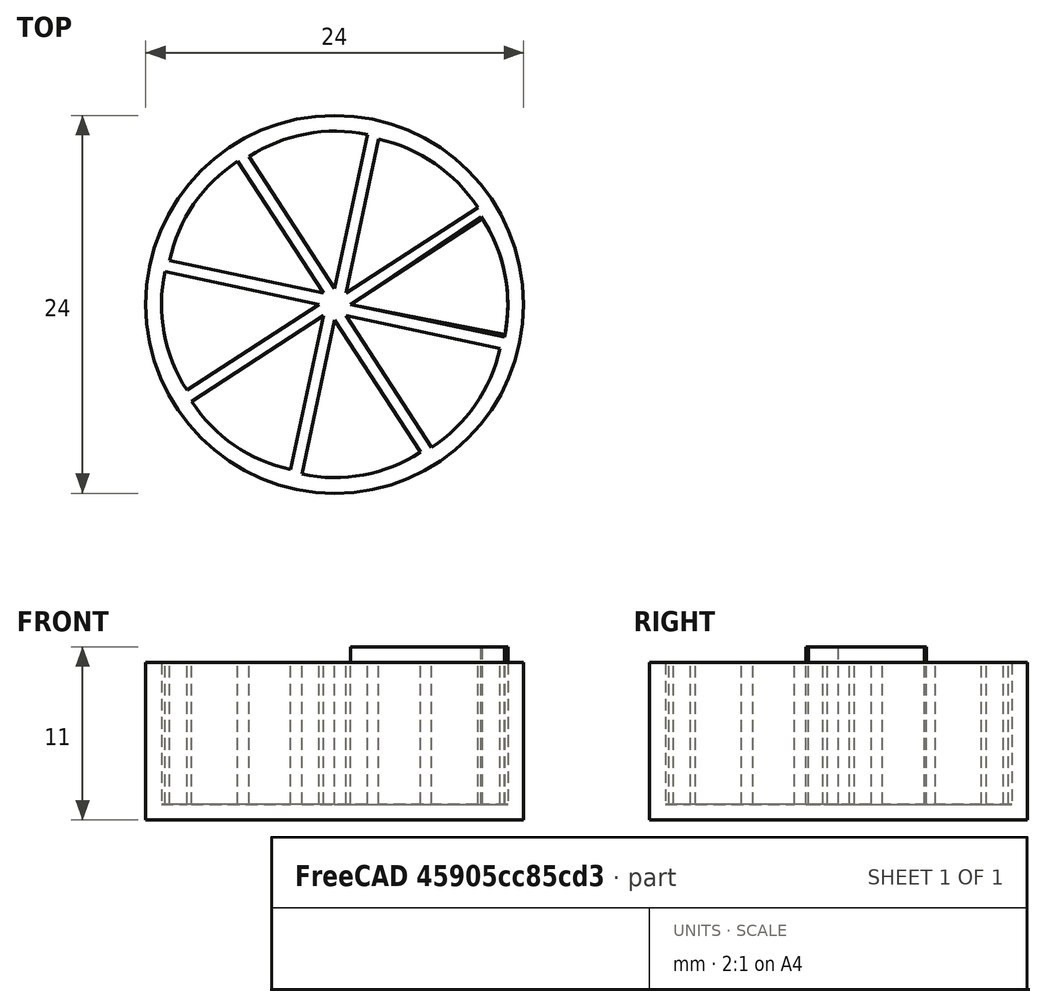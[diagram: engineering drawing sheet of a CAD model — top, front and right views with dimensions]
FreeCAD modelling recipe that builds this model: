
FCSTD DOCUMENT  (FreeCAD 0.21R33694 (Git))
Label: OJT1_T11R02_trivial
License: All rights reserved
LicenseURL: https://en.wikipedia.org/wiki/All_rights_reserved
objects: Part::Cylinder×3, Part::FeaturePython×1, Part::Cut×1
note: 4 computed .brp shape members not serialized (recipe doc carries the construction recipe); baked Part::Feature solids carry a one-line shape summary decoded from their .brp

FEATURE [Part::Cylinder] Cylinder  label="Base"
  Angle = 360
  AttacherType = Attacher::AttachEngine3D
  FirstAngle = 0
  Height = 10
  Placement = pos=(0,0,-1) rot=(0,0,1;0rad)
  Radius = 12
  SecondAngle = 0
FEATURE [Part::Cylinder] Cylinder001  label="Cilindre001"
  Angle = 45
  AttacherType = Attacher::AttachEngine3D
  FirstAngle = 0
  Height = 10
  Placement = pos=(1,0,0) rot=(0,0,1;-0.20944rad)
  Radius = 10
  SecondAngle = 0
FEATURE [Part::FeaturePython] Array  label="Triangles petits"  # Draft array (typed FeaturePython)
  AlwaysSyncPlacement = false
  Angle = 360
  ArrayType = 1
  Axis = (0,0,1)
  Base = -> Cylinder001
  Center = (0,0,0)
  Count = 8
  ExpandArray = false
  Fuse = false
  IntervalAxis = (0,0,0)
  IntervalX = (100,0,0)
  IntervalY = (0,100,0)
  IntervalZ = (0,0,100)
  NumberCircles = 3
  NumberPolar = 8
  NumberX = 2
  NumberY = 2
  NumberZ = 1
  PlacementList = 8 placements: [(1,0,0),(0.707107,0.707107,0),(0,1,0),(-0.707107,0.707107,0),(-1,1.22465e-16,0),(-0.707107,-0.707107,0),(-2.22045e-16,-1,0),(0.707107,-0.707107,0)]
  RadialDistance = 50
  ScaleList = (8) [(1,1,1),(1,1,1),(1,1,1),(1,1,1),(1,1,1),(1,1,1),(1,1,1),(1,1,1)]
  Symmetry = 1
  TangentialDistance = 25
FEATURE [Part::Cut] Cut  label="BASE"
  Base = -> Cylinder
  Tool = -> Array
FEATURE [Part::Cylinder] Cylinder002  label="Cilindre"
  Angle = 45
  AttacherType = Attacher::AttachEngine3D
  FirstAngle = 0
  Height = 10
  Placement = pos=(1,0,0) rot=(0,0,-1;0.191986rad)
  Radius = 10
  SecondAngle = 0
